# Revit family: Sink-Undermount-Lavatory-KOHLER-Derring-K-17889BR_1
name_source: partatom
category: Plumbing Fixtures
revit_build: Autodesk Revit 2017 (Build: 20160225_1515(x64)
units: mm (PartAtom-declared; Revit-internal decimal feet)

## family parameters
Cut with Voids When Loaded = No
Host = Face
OmniClass Number = 23.31.13.00
OmniClass Title = Sinks
Part Type = Normal
Room Calculation Point = No
Round Connector Dimension = Use Diameter
Shared = No

## types (2) — shared parameters
ADA Compliant = No
Assembly Code = D2010400
CW Connection = No
Cold Water Inlet = Cold Water Inlet
Date Modified = 05/17/2021
Default Elevation = 36"
Description = Derring Design Oval built-in washbasin 492 x 416mm
Drain Included = No
HW Connection = No
Height = 7 3/16"
Hot Water Inlet = Hot Water Inlet
Length = 16 3/8"
Manufacturer = KOHLER Co.
Master Format 2014 = 22 41 16
Master Format 2014 Name = Residential Lavatories and Sinks
Material = Vitreous China
Product Documentation Link = http://resources.kohler.com
Product Name = Derring
Product Page URL = https://br.kohler.com
URL = https://br.kohler.com
Vent Connection = No
Waste Connection = Yes
Waste Water Outlet = Waste Water Outlet
WaterSense Certified = No
Width = 19 3/8"

## per-type parameters (varying)
| type | Finish | Model | Type |
| K8-Translucent White | Kohler-Vitreous_China-K8-Translucent_White | K-17889BR-RL-K8 | 1 |
| RB2-Bourbon Rutile | Kohler-Vitreous_China-RB2-Bourbon_Rutile | K-17889BR-RL-RB2 | 2 |

## geometry (parser evidence)
native form markers: Sweep x4
no freeform markers — native parametric forms only
